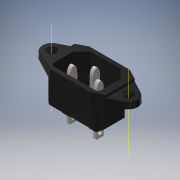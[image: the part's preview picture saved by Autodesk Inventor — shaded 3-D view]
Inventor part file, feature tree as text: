
AUTODESK INVENTOR PART (.ipt)
format: ipt  version: 2018 (Build 220112000, 112)  size: 710,144 bytes
history: native  units: mm
features: other x5, plane x1, fillet x1
ambient origin geometry x8: Origin, YZ Plane, XZ Plane, XY Plane, X Axis, Y Axis, Z Axis, Center Point
bodies: Solid1 (feature_tree), Solid2 (feature_tree), Solid3 (feature_tree), Solid4 (feature_tree)
feature tree (7):
  other  "Work Axis1"
  other  "Work Axis2"
  plane  "Work Plane1"
  other  "Saliente-Extruir3"
  fillet  "Redondeo7"  [1 undecoded]
  other  "Sólido-Mover_Copiar1"
  other  "Sólido-Mover_Copiar2"
note: 1 required parameter value undecoded (feature->parameter linkage not recoverable at this tier; creation-order binding heuristic only, values carry confidence <= 0.55)
